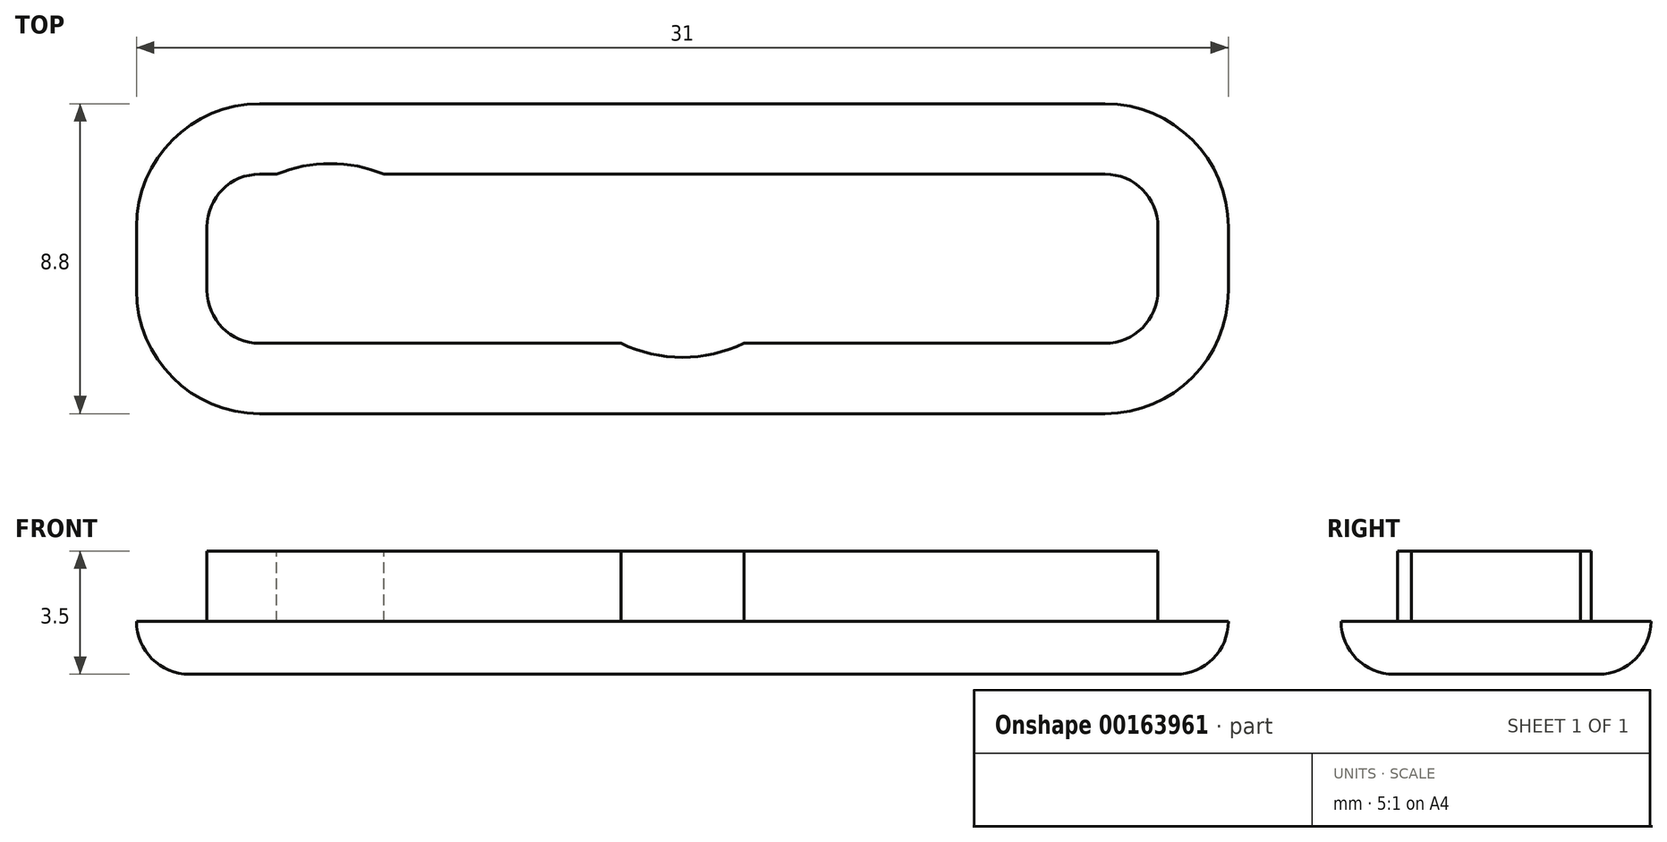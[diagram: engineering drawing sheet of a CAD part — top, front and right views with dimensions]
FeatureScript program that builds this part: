
annotation { "Feature Type Name" : "Feature", "Feature Type Description" : "" }
export const myFeature = defineFeature(function(context is Context, id is Id, definition is map)
    precondition{}
    {
        {
            var Q0;
            Q0=qCreatedBy(makeId("Top.planeOp"),FACE);
            var sketch = newSketch(context, id + "F0", { "sketchPlane" : qUnion([Q0])});
            skLineSegment(sketch, "E0.bottom", {"start": v(12, -2.4) * mm, "end": v(-12, -2.4) * mm});
            skLineSegment(sketch, "E0.top", {"start": v(12, 2.4) * mm, "end": v(-12, 2.4) * mm});
            skLineSegment(sketch, "E0.left", {"start": v(13.5, -0.9) * mm, "end": v(13.5, 0.9) * mm});
            skLineSegment(sketch, "E0.right", {"start": v(-13.5, -0.9) * mm, "end": v(-13.5, 0.9) * mm});
            skPoint(sketch, "E0.middle", {"position": v(0, 0) * mm});
            skPoint(sketch, "E1.visualSharp", {"position": v(-13.5, 2.4) * mm});
            skArc(sketch, "E1.filletArc", {"start": v(-12, 2.4) * mm, "mid": v(-13.06, 1.96) * mm, "end": v(-13.5, 0.9) * mm});
            skPoint(sketch, "E2.visualSharp", {"position": v(-13.5, -2.4) * mm});
            skArc(sketch, "E2.filletArc", {"start": v(-13.5, -0.9) * mm, "mid": v(-13.06, -1.96) * mm, "end": v(-12, -2.4) * mm});
            skPoint(sketch, "E3.visualSharp", {"position": v(13.5, 2.4) * mm});
            skArc(sketch, "E3.filletArc", {"start": v(13.5, 0.9) * mm, "mid": v(13.06, 1.96) * mm, "end": v(12, 2.4) * mm});
            skPoint(sketch, "E4.visualSharp", {"position": v(13.5, -2.4) * mm});
            skArc(sketch, "E4.filletArc", {"start": v(12, -2.4) * mm, "mid": v(13.06, -1.96) * mm, "end": v(13.5, -0.9) * mm});
            skArc(sketch, "E5.0", {"start": v(15.5, 0.9) * mm, "mid": v(14.47, 3.37) * mm, "end": v(12, 4.4) * mm});
            skLineSegment(sketch, "E5.1", {"start": v(15.5, -0.9) * mm, "end": v(15.5, 0.9) * mm});
            skLineSegment(sketch, "E5.2", {"start": v(12, 4.4) * mm, "end": v(-12, 4.4) * mm});
            skArc(sketch, "E5.3", {"start": v(12, -4.4) * mm, "mid": v(14.47, -3.37) * mm, "end": v(15.5, -0.9) * mm});
            skArc(sketch, "E5.4", {"start": v(-12, 4.4) * mm, "mid": v(-14.47, 3.37) * mm, "end": v(-15.5, 0.9) * mm});
            skLineSegment(sketch, "E5.5", {"start": v(-15.5, -0.9) * mm, "end": v(-15.5, 0.9) * mm});
            skArc(sketch, "E5.6", {"start": v(-15.5, -0.9) * mm, "mid": v(-14.47, -3.37) * mm, "end": v(-12, -4.4) * mm});
            skLineSegment(sketch, "E5.7", {"start": v(12, -4.4) * mm, "end": v(-12, -4.4) * mm});
            skArc(sketch, "E6.0", {"start": v(12.7, 0.9) * mm, "mid": v(12.5, 1.4) * mm, "end": v(12, 1.6) * mm});
            skLineSegment(sketch, "E6.1", {"start": v(12.7, -0.9) * mm, "end": v(12.7, 0.9) * mm});
            skLineSegment(sketch, "E6.2", {"start": v(12, 1.6) * mm, "end": v(-12, 1.6) * mm});
            skArc(sketch, "E6.3", {"start": v(12, -1.6) * mm, "mid": v(12.5, -1.4) * mm, "end": v(12.7, -0.9) * mm});
            skArc(sketch, "E6.4", {"start": v(-12, 1.6) * mm, "mid": v(-12.5, 1.4) * mm, "end": v(-12.7, 0.9) * mm});
            skLineSegment(sketch, "E6.5", {"start": v(-12.7, -0.9) * mm, "end": v(-12.7, 0.9) * mm});
            skArc(sketch, "E6.6", {"start": v(-12.7, -0.9) * mm, "mid": v(-12.5, -1.4) * mm, "end": v(-12, -1.6) * mm});
            skLineSegment(sketch, "E6.7", {"start": v(12, -1.6) * mm, "end": v(-12, -1.6) * mm});
            skSolve(sketch);
        }
        {
            var Q0;
            Q0=makeQuery(id+"F0.imprint","IMPRINT",FACE,{"disambiguationData":[TD([[makeQuery(id+"F0.imprint","IMPRINT",EDGE,{"derivedFrom":sQuery(id+"F0.wireOp",EDGE,"E0.bottom")}),1.0]])]});
            var Q1;
            Q1=makeQuery(id+"F0.imprint","IMPRINT",FACE,{"disambiguationData":[TD([[makeQuery(id+"F0.imprint","IMPRINT",EDGE,{"derivedFrom":sQuery(id+"F0.wireOp",EDGE,"E6.0")}),1.0]])]});
            var Q2;
            Q2=makeQuery(id+"F0.imprint","IMPRINT",FACE,{"disambiguationData":[TD([[makeQuery(id+"F0.imprint","IMPRINT",EDGE,{"derivedFrom":sQuery(id+"F0.wireOp",EDGE,"E0.bottom")}),-1.0]])]});
            extrude(context, id + "F1", {"entities" : qUnion([Q0, Q1, Q2]), "depth" : 1.5 * mm});
        }
        {
            var Q0;
            Q0=makeQuery(id+"F0.imprint","IMPRINT",FACE,{"disambiguationData":[TD([[makeQuery(id+"F0.imprint","IMPRINT",EDGE,{"derivedFrom":sQuery(id+"F0.wireOp",EDGE,"E0.bottom")}),-1.0]])]});
            var Q1;
            Q1=makeQuery(id+"F0.imprint","IMPRINT",FACE,{"disambiguationData":[TD([[makeQuery(id+"F0.imprint","IMPRINT",EDGE,{"derivedFrom":sQuery(id+"F0.wireOp",EDGE,"E6.0")}),1.0]])]});
            extrude(context, id + "F2", {"entities" : qUnion([Q0, Q1]), "operationType" : NewBodyOperationType.ADD, "depth" : 3.5 * mm});
        }
        {
            var Q0;
            Q0=makeQuery(id+"F1.opExtrude","CAP_EDGE",EDGE,{"disambiguationData":[OSD([sQuery(id+"F0.wireOp",EDGE,"E5.7")])],"isStart":true});
            var Q1;
            Q1=makeQuery(id+"F1.opExtrude","CAP_EDGE",EDGE,{"disambiguationData":[OSD([sQuery(id+"F0.wireOp",EDGE,"E5.6")])],"isStart":true});
            var Q2;
            Q2=makeQuery(id+"F1.opExtrude","CAP_EDGE",EDGE,{"disambiguationData":[OSD([sQuery(id+"F0.wireOp",EDGE,"E5.5")])],"isStart":true});
            fillet(context, id + "F3", {"entities" : qUnion([Q0, Q1, Q2]), "radius" : 1.5 * mm, "tangentPropagation" : true, "allowEdgeOverflow" : false});
        }
        {
            var Q0;
            Q0=makeQuery(id+"F2.opExtrude","CAP_FACE",FACE,{"disambiguationData":[OSD([sQuery(id+"F0.wireOp",EDGE,"E0.bottom"),sQuery(id+"F0.wireOp",EDGE,"E0.top"),sQuery(id+"F0.wireOp",EDGE,"E0.left"),sQuery(id+"F0.wireOp",EDGE,"E0.right"),sQuery(id+"F0.wireOp",EDGE,"E1.filletArc"),sQuery(id+"F0.wireOp",EDGE,"E2.filletArc"),sQuery(id+"F0.wireOp",EDGE,"E3.filletArc"),sQuery(id+"F0.wireOp",EDGE,"E4.filletArc")])],"isStart":false});
            var sketch = newSketch(context, id + "F4", { "sketchPlane" : qUnion([Q0])});
            skCircle(sketch, "E7", {"center": v(-10, -1.3) * mm, "radius": 4 * mm});
            skCircle(sketch, "E8.MirrorC", {"center": v(10, -1.3) * mm, "radius": 4 * mm});
            skCircle(sketch, "E9", {"center": v(0, 1.2) * mm, "radius": 4 * mm});
            skSolve(sketch);
        }
        {
            var Q0;
            {var subQ0=sQuery(id+"F4.wireOp",EDGE,"E7");var subQ1=makeQuery(id+"F2.opExtrude","CAP_EDGE",EDGE,{"disambiguationData":[OSD([sQuery(id+"F0.wireOp",EDGE,"E0.top")])],"isStart":false});var subQ2=makeQuery(id+"F4.imprint","INTERSECT",VERTEX,{"disambiguationData":[OD(0.0)],"derivedFrom":[subQ1,subQ0]});Q0=makeQuery(id+"F4.imprint","IMPRINT",FACE,{"disambiguationData":[TD([[makeQuery(id+"F4.imprint","IMPRINT",EDGE,{"disambiguationData":[TD([[subQ2,1.0]])],"derivedFrom":subQ0}),1.0]])]});}
            var Q1;
            {var subQ0=sQuery(id+"F4.wireOp",EDGE,"E9");var subQ1=makeQuery(id+"F2.opExtrude","CAP_EDGE",EDGE,{"disambiguationData":[OSD([sQuery(id+"F0.wireOp",EDGE,"E0.bottom")])],"isStart":false});var subQ2=makeQuery(id+"F4.imprint","INTERSECT",VERTEX,{"disambiguationData":[OD(0.0)],"derivedFrom":[subQ1,subQ0]});Q1=makeQuery(id+"F4.imprint","IMPRINT",FACE,{"disambiguationData":[TD([[makeQuery(id+"F4.imprint","IMPRINT",EDGE,{"disambiguationData":[TD([[subQ2,-1.0]])],"derivedFrom":subQ0}),1.0]])]});}
            var Q2;
            {var subQ0=sQuery(id+"F4.wireOp",EDGE,"E8.MirrorC");var subQ1=makeQuery(id+"F2.opExtrude","CAP_EDGE",EDGE,{"disambiguationData":[OSD([sQuery(id+"F0.wireOp",EDGE,"E0.top")])],"isStart":false});var subQ2=makeQuery(id+"F4.imprint","INTERSECT",VERTEX,{"disambiguationData":[OD(0.0)],"derivedFrom":[subQ1,subQ0]});Q2=makeQuery(id+"F4.imprint","IMPRINT",FACE,{"disambiguationData":[TD([[makeQuery(id+"F4.imprint","IMPRINT",EDGE,{"disambiguationData":[TD([[subQ2,1.0]])],"derivedFrom":subQ0}),-1.0]])]});}
            var Q3;
            Q3=makeQuery(id+"F1.opExtrude","CAP_FACE",FACE,{"disambiguationData":[OSD([sQuery(id+"F0.wireOp",EDGE,"E5.0"),sQuery(id+"F0.wireOp",EDGE,"E5.1"),sQuery(id+"F0.wireOp",EDGE,"E5.2"),sQuery(id+"F0.wireOp",EDGE,"E5.3"),sQuery(id+"F0.wireOp",EDGE,"E5.4"),sQuery(id+"F0.wireOp",EDGE,"E5.5"),sQuery(id+"F0.wireOp",EDGE,"E5.6"),sQuery(id+"F0.wireOp",EDGE,"E5.7")])],"isStart":false});
            extrude(context, id + "F5", {"entities" : qUnion([Q0, Q1, Q2]), "operationType" : NewBodyOperationType.ADD, "endBound" : BoundingType.UP_TO_SURFACE, "oppositeDirection" : true, "endBoundEntityFace" : qUnion([Q3]), "depth" : 25 * mm});
        }
    });
